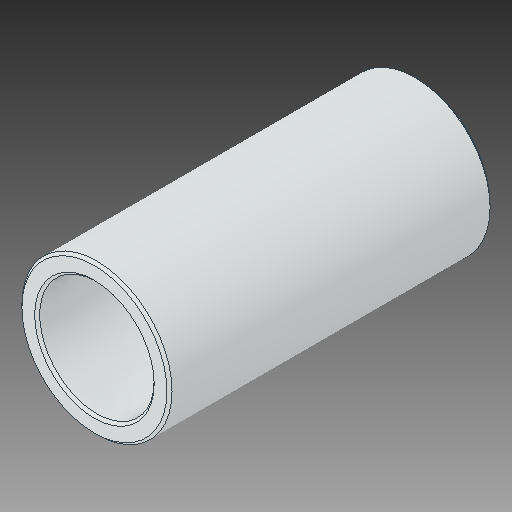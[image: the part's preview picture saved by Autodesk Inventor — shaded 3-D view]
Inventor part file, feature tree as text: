
AUTODESK INVENTOR PART (.ipt)
format: ipt  version: 2017 (Build 210142000, 142)  size: 115,712 bytes
history: native  units: in
note: dims shown in document units (in); Inventor stores cm internally (conversion verified against a paired STEP export)
features: chamfer x1
ambient origin geometry x8: Origin, YZ Plane, XZ Plane, XY Plane, X Axis, Y Axis, Z Axis, Center Point
bodies: Solid1 (feature_tree)
feature tree (1):
  chamfer  "Chamfer1"  [1 undecoded]
note: 1 required parameter value undecoded (feature->parameter linkage not recoverable at this tier; creation-order binding heuristic only, values carry confidence <= 0.55)
